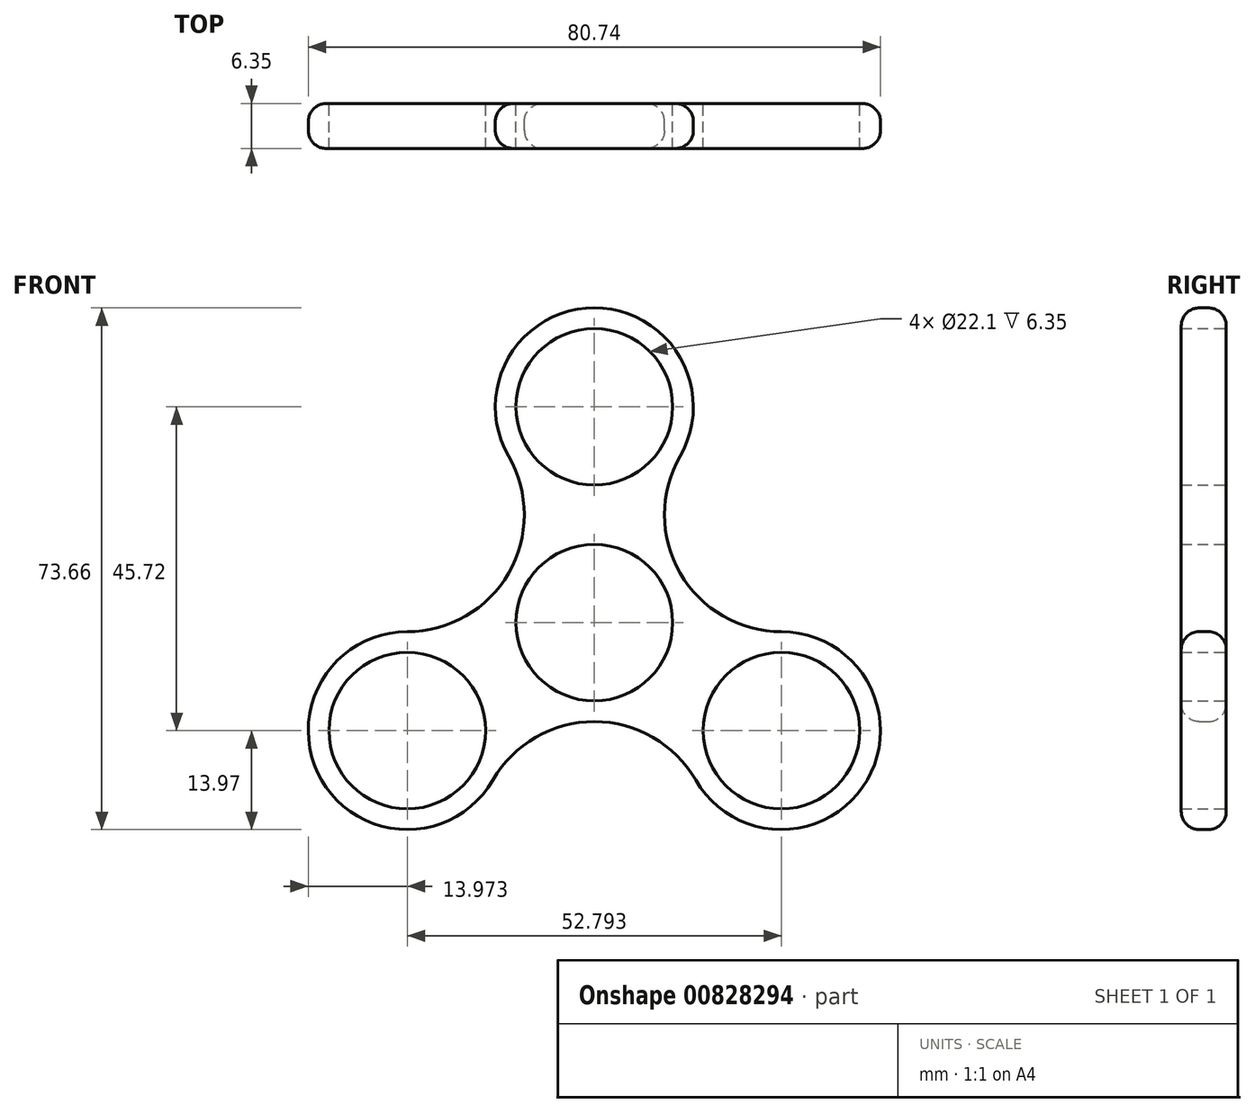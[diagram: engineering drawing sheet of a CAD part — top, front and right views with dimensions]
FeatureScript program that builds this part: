
annotation { "Feature Type Name" : "Feature", "Feature Type Description" : "" }
export const myFeature = defineFeature(function(context is Context, id is Id, definition is map)
    precondition{}
    {
        {
            var Q0;
            Q0=qCreatedBy(makeId("Front.planeOp"),FACE);
            var sketch = newSketch(context, id + "F0", { "sketchPlane" : qUnion([Q0])});
            skCircle(sketch, "E0", {"center": v(0, 0) * mm, "radius": 11.05 * mm});
            skCircle(sketch, "E1", {"center": v(0, 30.48) * mm, "radius": 11.05 * mm});
            skArc(sketch, "E2", {"start": v(12.1, 23.5) * mm, "mid": v(0, 44.45) * mm, "end": v(-12.1, 23.5) * mm});
            skArc(sketch, "E3.1.0", {"start": v(-26.4, -1.27) * mm, "mid": v(-38.5, -22.22) * mm, "end": v(-14.3, -22.23) * mm});
            skCircle(sketch, "E3.1.2", {"center": v(-26.4, -15.24) * mm, "radius": 11.05 * mm});
            skArc(sketch, "E3.2.0", {"start": v(14.3, -22.22) * mm, "mid": v(38.5, -22.23) * mm, "end": v(26.4, -1.27) * mm});
            skCircle(sketch, "E3.2.2", {"center": v(26.4, -15.24) * mm, "radius": 11.05 * mm});
            skArc(sketch, "E4", {"start": v(-26.4, -1.27) * mm, "mid": v(-12.1, 6.99) * mm, "end": v(-12.1, 23.5) * mm});
            skArc(sketch, "E5.1.0", {"start": v(14.3, -22.23) * mm, "mid": v(0, -13.97) * mm, "end": v(-14.3, -22.22) * mm});
            skArc(sketch, "E5.2.0", {"start": v(12.1, 23.5) * mm, "mid": v(12.1, 6.98) * mm, "end": v(26.4, -1.27) * mm});
            skSolve(sketch);
        }
        {
            var Q0;
            Q0=makeQuery(id+"F0.imprint","IMPRINT",FACE,{"disambiguationData":[TD([[makeQuery(id+"F0.imprint","IMPRINT",EDGE,{"derivedFrom":sQuery(id+"F0.wireOp",EDGE,"E0")}),-1.0]])]});
            extrude(context, id + "F1", {"entities" : qUnion([Q0]), "depth" : 6.35 * mm, "offsetDistance" : 25.4 * mm});
        }
        {
            var Q0;
            Q0=makeQuery(id+"F1.opExtrude","CAP_EDGE",EDGE,{"disambiguationData":[OSD([sQuery(id+"F0.wireOp",EDGE,"E4")])],"isStart":true});
            var Q1;
            Q1=makeQuery(id+"F1.opExtrude","CAP_EDGE",EDGE,{"disambiguationData":[OSD([sQuery(id+"F0.wireOp",EDGE,"E5.1.0")])],"isStart":false});
            fillet(context, id + "F2", {"entities" : qUnion([Q0, Q1]), "radius" : 2.54 * mm, "tangentPropagation" : true, "allowEdgeOverflow" : false});
        }
    });
